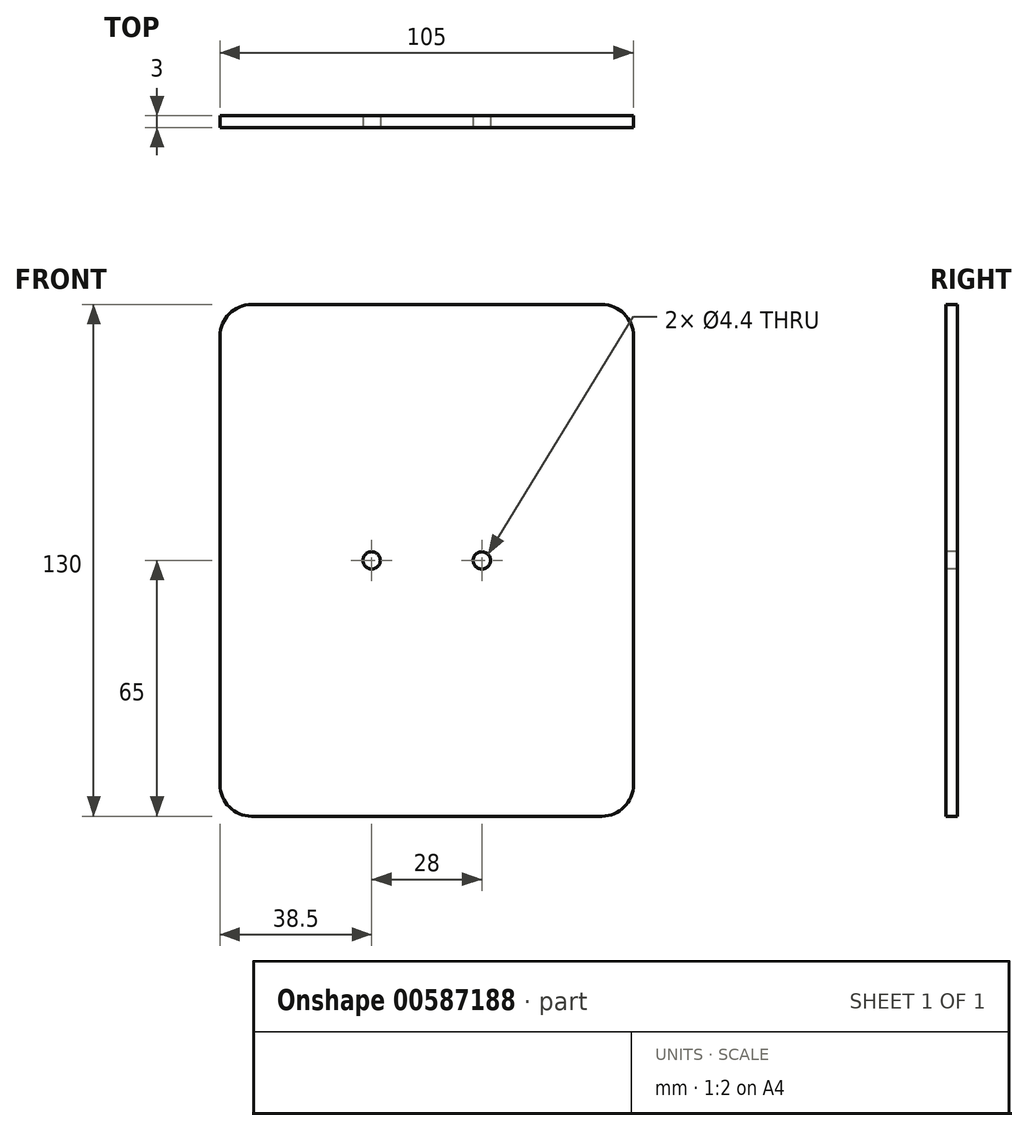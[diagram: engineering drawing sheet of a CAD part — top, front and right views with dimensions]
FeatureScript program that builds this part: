
annotation { "Feature Type Name" : "Feature", "Feature Type Description" : "" }
export const myFeature = defineFeature(function(context is Context, id is Id, definition is map)
    precondition{}
    {
        {
            var Q0;
            Q0=qCreatedBy(makeId("Front.planeOp"),FACE);
            var sketch = newSketch(context, id + "F0", { "sketchPlane" : qUnion([Q0])});
            skLineSegment(sketch, "E0.bottom", {"start": v(52.5, 65) * mm, "end": v(-52.5, 65) * mm});
            skLineSegment(sketch, "E0.top", {"start": v(52.5, -65) * mm, "end": v(-52.5, -65) * mm});
            skLineSegment(sketch, "E0.left", {"start": v(52.5, 65) * mm, "end": v(52.5, -65) * mm});
            skLineSegment(sketch, "E0.right", {"start": v(-52.5, 65) * mm, "end": v(-52.5, -65) * mm});
            skPoint(sketch, "E0.middle", {"position": v(0, 0) * mm});
            skSolve(sketch);
        }
        {
            var Q0;
            Q0 = qSketchRegion(id + "F0", true);
            extrude(context, id + "F1", {"entities" : qUnion([Q0]), "depth" : 3 * mm, "offsetDistance" : 25 * mm});
        }
        {
            var Q0;
            Q0=makeQuery(id+"F1.opExtrude","CAP_FACE",FACE,{"disambiguationData":[OSD([sQuery(id+"F0.wireOp",EDGE,"E0.bottom"),sQuery(id+"F0.wireOp",EDGE,"E0.top"),sQuery(id+"F0.wireOp",EDGE,"E0.left"),sQuery(id+"F0.wireOp",EDGE,"E0.right")])],"isStart":false});
            var sketch = newSketch(context, id + "F2", { "sketchPlane" : qUnion([Q0])});
            skLineSegment(sketch, "E1", {"start": v(-14, 0) * mm, "end": v(14, 0) * mm, "construction": true});
            skSolve(sketch);
        }
        {
            var Q0;
            Q0=sQuery(id+"F2.wireOp",VERTEX,"E1.start");
            var Q1;
            Q1=sQuery(id+"F2.wireOp",VERTEX,"E1.end");
            var Q2;
            Q2=makeQuery(id+"F1.opExtrude","SWEPT_BODY",BODY,{"disambiguationData":[OSD([sQuery(id+"F0.wireOp",EDGE,"E0.bottom"),sQuery(id+"F0.wireOp",EDGE,"E0.top"),sQuery(id+"F0.wireOp",EDGE,"E0.left"),sQuery(id+"F0.wireOp",EDGE,"E0.right")])]});
            hole(context, id + "F3", {"style" : HoleStyle.SIMPLE, "endStyle" : HoleEndStyle.THROUGH, "standardTappedOrClearance" : lookupTablePath({ "standard" : "ISO", "fit" : "Normal", "size" : "M4", "type" : "Clearance" }), "standardBlindInLast" : lookupTablePath({ "fit" : "Standard", "standard" : "ISO", "size" : "M4", "type" : "Clearance" }), "holeDiameter" : 4.4 * mm, "majorDiameter" : 5 * mm, "isTappedThrough" : true, "tappedDepth" : 12 * mm, "tapClearance" : 3, "locations" : qUnion([Q0, Q1]), "scope" : qUnion([Q2])});
        }
        {
            var Q0;
            Q0=makeQuery(id+"F1.opExtrude","SWEPT_EDGE",EDGE,{"disambiguationData":[OSD([sQuery(id+"F0.wireOp",EDGE,"E0.bottom"),sQuery(id+"F0.wireOp",EDGE,"E0.left")])]});
            var Q1;
            Q1=makeQuery(id+"F1.opExtrude","SWEPT_EDGE",EDGE,{"disambiguationData":[OSD([sQuery(id+"F0.wireOp",EDGE,"E0.bottom"),sQuery(id+"F0.wireOp",EDGE,"E0.right")])]});
            var Q2;
            Q2=makeQuery(id+"F1.opExtrude","SWEPT_EDGE",EDGE,{"disambiguationData":[OSD([sQuery(id+"F0.wireOp",EDGE,"E0.top"),sQuery(id+"F0.wireOp",EDGE,"E0.right")])]});
            var Q3;
            Q3=makeQuery(id+"F1.opExtrude","SWEPT_EDGE",EDGE,{"disambiguationData":[OSD([sQuery(id+"F0.wireOp",EDGE,"E0.top"),sQuery(id+"F0.wireOp",EDGE,"E0.left")])]});
            fillet(context, id + "F4", {"entities" : qUnion([Q0, Q1, Q2, Q3]), "radius" : 8 * mm, "tangentPropagation" : true, "allowEdgeOverflow" : false});
        }
    });
